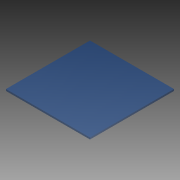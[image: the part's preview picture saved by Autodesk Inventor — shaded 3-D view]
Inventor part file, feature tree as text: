
AUTODESK INVENTOR PART (.ipt)
format: ipt  version: 2015 (Build 190159000, 159)  size: 86,528 bytes
history: native  units: mm
features: other x1, extrude x1, sketch x1
ambient origin geometry x8: Origin, YZ Plane, XZ Plane, XY Plane, X Axis, Y Axis, Z Axis, Center Point
bodies: Body1 (feature_tree)
feature tree (3):
  other  "ソリッド1"
  extrude  "押し出し1"  Depth=500.0mm
  sketch  "スケッチ1"
